FCSTD DOCUMENT  (FreeCAD 0.21R33771 (Git))
Label: radar
License: All rights reserved
LicenseURL: https://en.wikipedia.org/wiki/All_rights_reserved
objects: Part::FeaturePython×6, PartDesign::ShapeBinder×2, Part::Cylinder×1, Part::Cut×1, PartDesign::Body×1, App::Part×1
note: 11 computed .brp shape members not serialized (recipe doc carries the construction recipe); baked Part::Feature solids carry a one-line shape summary decoded from their .brp

FEATURE [Part::FeaturePython] b_radar_001_  label="radar_001"  # a2plus imported part (geometry in sourceFile) (typed FeaturePython)
  a2p_Version = 0.4.65
  fixedPosition = true
  objectType = a2pPart
  sourceFile = .\radar.FCStd
  subassemblyImport = false
  timeLastImport = 1.7241e+09
  updateColors = true
FEATURE [Part::FeaturePython] b_scren_top_001_  label="scren_top_001"  # a2plus imported part (geometry in sourceFile) (typed FeaturePython)
  Placement = pos=(45.7639,-21.8345,-0.518072) rot=(0,0,1;1.5708rad)
  a2p_Version = 0.4.65
  fixedPosition = false
  objectType = a2pPart
  sourceFile = .\scren_top.FCStd
  subassemblyImport = false
  timeLastImport = 1.7241e+09
  updateColors = true
FEATURE [Part::FeaturePython] b_Radar_ant_001_  label="Radar_ant_001"  # a2plus imported part (geometry in sourceFile) (typed FeaturePython)
  Placement = pos=(0.583369,-38.5915,-0.00412369) rot=(1,0,0;3.14159rad)
  a2p_Version = 0.4.65
  fixedPosition = false
  objectType = a2pPart
  sourceFile = .\Radar_ant.FCStd
  subassemblyImport = false
  timeLastImport = 1.7241e+09
  updateColors = true
FEATURE [Part::FeaturePython] b_scren_bot_001_  label="scren_bot_001"  # a2plus imported part (geometry in sourceFile) (typed FeaturePython)
  Placement = pos=(46.2874,-22.0715,-0.151866) rot=(1,0,0;3.14159rad)
  a2p_Version = 0.4.65
  fixedPosition = false
  objectType = a2pPart
  sourceFile = .\scren_bot.FCStd
  subassemblyImport = false
  timeLastImport = 1.7241e+09
  updateColors = true
FEATURE [PartDesign::ShapeBinder] Copyb_Radar_ant_001_
  Placement = pos=(0.583369,-38.5915,-0.00412369) rot=(1,0,0;3.14159rad)
  TraceSupport = false
FEATURE [Part::Cylinder] Cylinder  label="Цилиндр"
  Angle = 360
  AttacherType = Attacher::AttachEngine3D
  FirstAngle = 0
  Height = 10
  Placement = pos=(2.6,-36.6,-10) rot=(0,0,1;0rad)
  Radius = 3
  SecondAngle = 0
FEATURE [Part::Cut] Cut
  Base = -> b_Radar_ant_001_
  Tool = -> Cylinder
FEATURE [Part::FeaturePython] b_laser_001_  label="laser_001"  # a2plus imported part (geometry in sourceFile) (typed FeaturePython)
  Placement = pos=(46.6484,-2.91862,-0.0349686) rot=(1,0,0;3.14159rad)
  a2p_Version = 0.4.65
  fixedPosition = false
  objectType = a2pPart
  sourceFile = .\laser.FCStd
  subassemblyImport = false
  timeLastImport = 1.72411e+09
  updateColors = true
FEATURE [PartDesign::ShapeBinder] CopyCut001
  Placement = pos=(28.8653,-17.9096,23.381) rot=(0,1,0;3.14159rad)
  TraceSupport = false
FEATURE [PartDesign::Body] Body
  Group = -> [Copyb_Radar_ant_001_,CopyCut001]
  Origin = -> Origin001
FEATURE [App::Part] Part
  Group = -> [Body,Cylinder,b_Radar_ant_001_,Cut]
  Origin = -> Origin
FEATURE [Part::FeaturePython] b_MB1_001_  label="MB1_001"  # a2plus imported part (geometry in sourceFile) (typed FeaturePython)
  Placement = pos=(9.8074,-41.8217,8.33313) rot=(0,0,1;1.5708rad)
  a2p_Version = 0.4.65
  fixedPosition = false
  objectType = a2pPart
  sourceFile = .\MB1.FCStd
  subassemblyImport = false
  timeLastImport = 1.72411e+09
  updateColors = true
